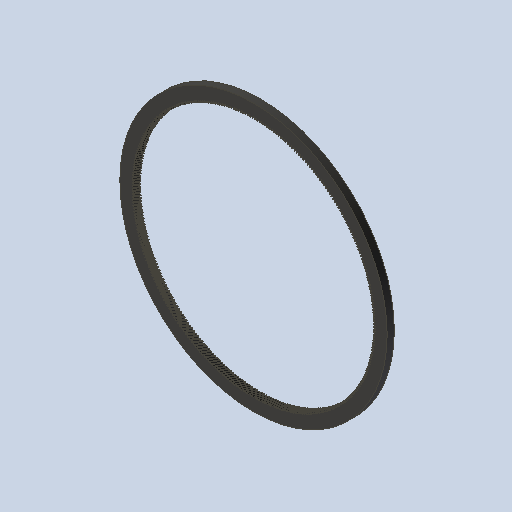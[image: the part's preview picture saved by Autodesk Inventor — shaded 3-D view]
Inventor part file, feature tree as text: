
AUTODESK INVENTOR PART (.ipt)
format: ipt  version: 2023 (Build 270158000, 158)  size: 3,464,192 bytes
history: native  units: mm (DEFAULTED — no unit token found)
features: plane x3, other x3, sketch x2, extrude x1
ambient origin geometry x8: Origin, YZ Plane, XZ Plane, XY Plane, X Axis, Y Axis, Z Axis, Center Point
bodies: Solid1 (feature_tree)
feature tree (9):
  extrude  "Extrusion1"  Depth=10.0mm TaperAngle=0.0deg
  plane  "Work Plane2"
  plane  "Work Plane8"
  plane  "Work Plane9"
  other  "Spur Gear"
  sketch  "Sketch1"  dims[d0=374.935695mm d1=10.0mm d2=0.0mm]
  sketch  "Sketch2"  dims[d3=338.408532mm d4=10.0mm d5=0.0mm d16=101.6mm d17=0.0mm d34=0.098792mm d39=0.0mm d45=0.0mm d47=101.6mm d50=0.0mm d51=0.0mm d52=101.6mm]
  other  "Srf1"
  other  "Pitch Diameter"
